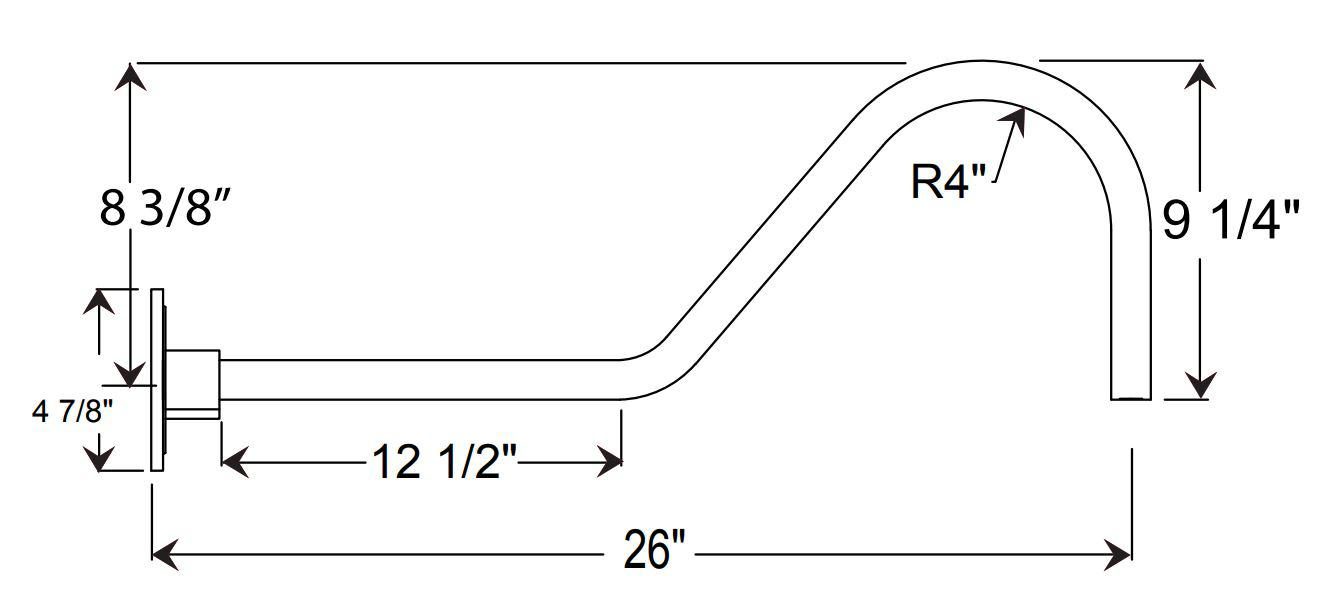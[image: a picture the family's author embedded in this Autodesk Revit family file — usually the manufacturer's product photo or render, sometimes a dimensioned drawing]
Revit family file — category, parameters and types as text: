
# Revit family: Satelite 9,19 LED
name_source: partatom
category: Lighting Fixtures
units: mm (PartAtom-declared; Revit-internal decimal feet)

## family parameters
Always vertical = Yes
Cut with Voids When Loaded = No
Light Source = Yes
OmniClass Number = 23.80.70.00
OmniClass Title = Lighting
Part Type = Normal
Room Calculation Point = No
Round Connector Dimension = Use Diameter
Shared = No
Work Plane-Based = No

## types (2) — shared parameters
Body Colour = Spun aluminium
Body Material = body
Bulb = Glass
CRI = >90
Canopy Body = body
Color Filter = 16777215
Construction Material = Heavy Duty spun aluminum.
Default Elevation = 0' - 0"
Description = 120-277 Voltage
Dimming = 1%
Dimming Lamp Color Temperature Shift = <None>
Efficiency = 65-125 lumens per watt
INSIDE BODY = Default
Lamp = LED
Life = L70 50,000 hours
Load Classification = Lighting
Manufacturer = ANP Lighting
Power Factor = 1
Tilt Angle = 90.00°
URL = https://www.anplighting.com
Voltage = 277 V
Warranty = 5 year limited warranty
b = 0' - 2"

## per-type parameters (varying)
| type | Apparent Load | Fixture Diameter | Fixture Height | Photometric Web File | SA09 | SA19 | Wattage Comments | Weight | a |
| SA9 | 16 VA | 0' - 9" | 0' - 9 1/4" | Generic.ies | Yes | No | 16 W | 6.0 lbs | 0' - 8" |
| SA19 | 24 VA | 1' - 7" | 1' - 0 1/2" | generic.ies | No | Yes | 24 W | 9.0 lbs | 0' - 11" |

note: column(s) folded — value = type name in every type: Model

## geometry (parser evidence)
native form markers: Sweep x24
no freeform markers — native parametric forms only
